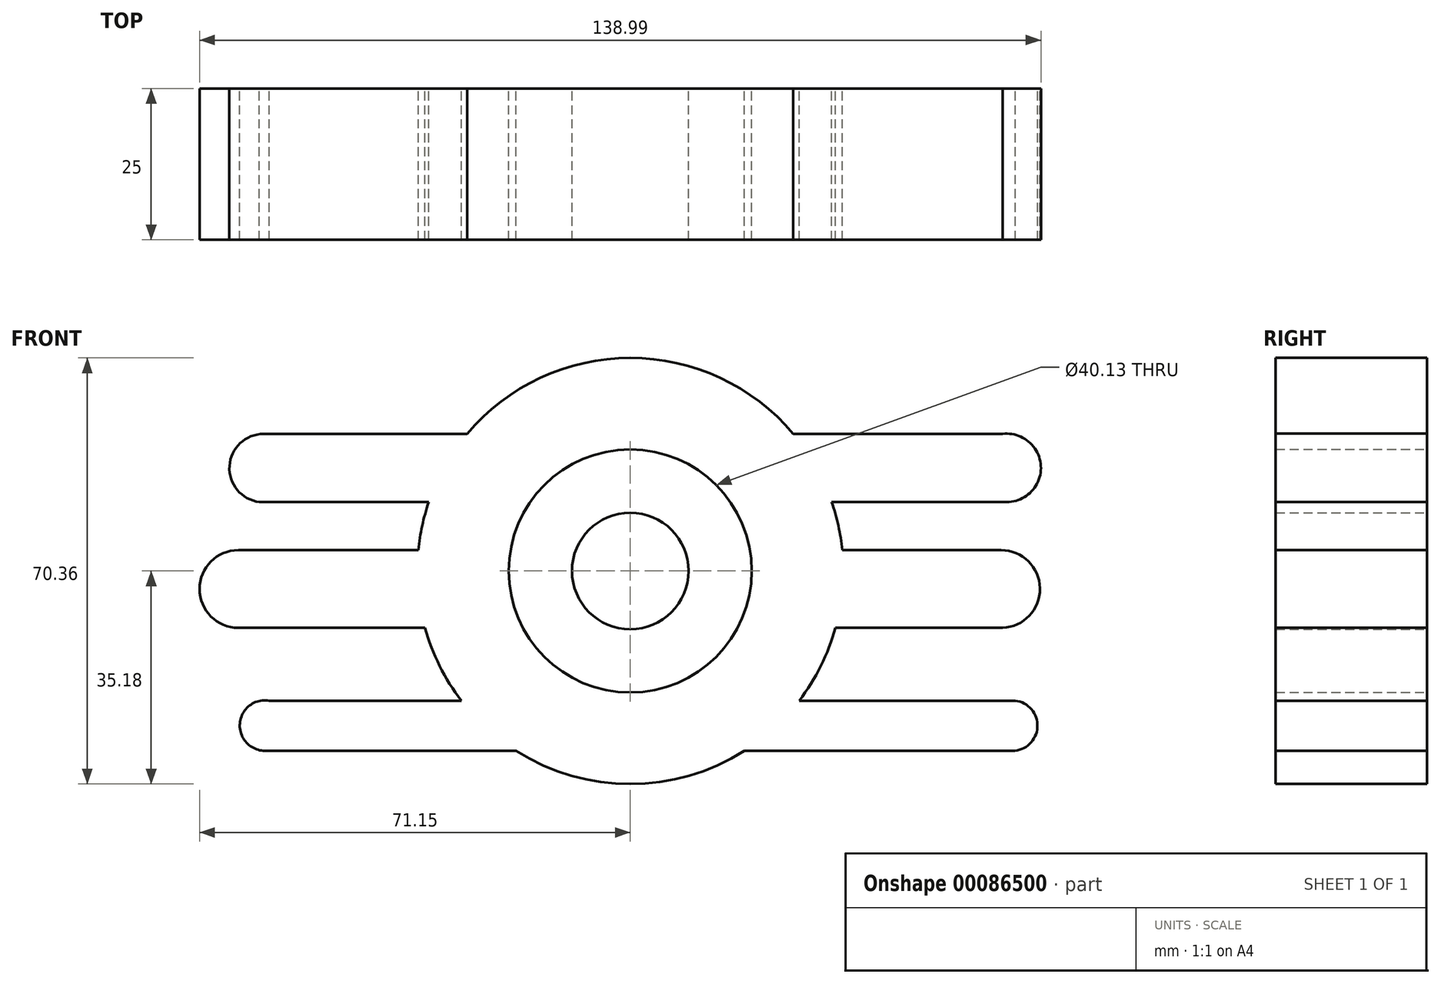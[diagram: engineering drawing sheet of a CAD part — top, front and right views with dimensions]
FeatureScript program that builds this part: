
annotation { "Feature Type Name" : "Feature", "Feature Type Description" : "" }
export const myFeature = defineFeature(function(context is Context, id is Id, definition is map)
    precondition{}
    {
        {
            var Q0;
            Q0=qCreatedBy(makeId("Front.planeOp"),FACE);
            var sketch = newSketch(context, id + "F0", { "sketchPlane" : qUnion([Q0])});
            skCircle(sketch, "E0", {"center": v(0, 0) * mm, "radius": 20.07 * mm});
            skCircle(sketch, "E1", {"center": v(0, 0) * mm, "radius": 35.18 * mm});
            skLineSegment(sketch, "E2", {"start": v(26.93, 22.63) * mm, "end": v(61.5, 22.63) * mm});
            skLineSegment(sketch, "E3", {"start": v(33.29, 11.38) * mm, "end": v(62.19, 11.38) * mm});
            skLineSegment(sketch, "E4", {"start": v(-26.93, 22.63) * mm, "end": v(-60.57, 22.63) * mm});
            skLineSegment(sketch, "E5", {"start": v(-33.29, 11.38) * mm, "end": v(-61.26, 11.38) * mm});
            skLineSegment(sketch, "E6", {"start": v(-35, 3.44) * mm, "end": v(-64.74, 3.44) * mm});
            skLineSegment(sketch, "E7", {"start": v(-33.9, -9.39) * mm, "end": v(-64.74, -9.39) * mm});
            skLineSegment(sketch, "E8", {"start": v(-27.9, -21.42) * mm, "end": v(-59.64, -21.42) * mm});
            skLineSegment(sketch, "E9", {"start": v(-18.86, -29.7) * mm, "end": v(-60.34, -29.7) * mm});
            skLineSegment(sketch, "E10", {"start": v(33.9, -9.39) * mm, "end": v(61.5, -9.39) * mm});
            skLineSegment(sketch, "E11", {"start": v(27.9, -21.42) * mm, "end": v(63.58, -21.42) * mm});
            skLineSegment(sketch, "E12", {"start": v(18.86, -29.7) * mm, "end": v(63.12, -29.7) * mm});
            skLineSegment(sketch, "E13", {"start": v(35, 3.44) * mm, "end": v(61.26, 3.44) * mm});
            skArc(sketch, "E14", {"start": v(-60.57, 22.63) * mm, "mid": v(-66.2, 17.33) * mm, "end": v(-61.26, 11.38) * mm});
            skArc(sketch, "E15", {"start": v(-64.74, 3.44) * mm, "mid": v(-71.15, -2.97) * mm, "end": v(-64.74, -9.39) * mm});
            skArc(sketch, "E16", {"start": v(-59.64, -21.42) * mm, "mid": v(-64.49, -25.18) * mm, "end": v(-60.34, -29.7) * mm});
            skArc(sketch, "E17", {"start": v(63.12, -29.7) * mm, "mid": v(67.26, -25.77) * mm, "end": v(63.58, -21.42) * mm});
            skArc(sketch, "E18", {"start": v(61.5, -9.39) * mm, "mid": v(67.68, -2.86) * mm, "end": v(61.26, 3.44) * mm});
            skArc(sketch, "E19", {"start": v(62.19, 11.38) * mm, "mid": v(67.83, 17.37) * mm, "end": v(61.5, 22.63) * mm});
            skCircle(sketch, "E20", {"center": v(0, 0) * mm, "radius": 9.62 * mm});
            skSolve(sketch);
        }
        {
            var Q0;
            Q0 = qSketchRegion(id + "F0", true);
            var Q1;
            Q1=makeQuery(id+"F0.imprint","IMPRINT",FACE,{"disambiguationData":[TD([[makeQuery(id+"F0.imprint","IMPRINT",EDGE,{"derivedFrom":sQuery(id+"F0.wireOp",EDGE,"E0")}),-1.0]])]});
            var Q2;
            Q2=makeQuery(id+"F0.imprint","IMPRINT",FACE,{"disambiguationData":[TD([[makeQuery(id+"F0.imprint","IMPRINT",EDGE,{"derivedFrom":sQuery(id+"F0.wireOp",EDGE,"E20")}),1.0]])]});
            extrude(context, id + "F1", {"entities" : qUnion([Q0, Q1, Q2]), "depth" : 25 * mm});
        }
    });
